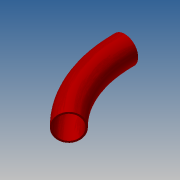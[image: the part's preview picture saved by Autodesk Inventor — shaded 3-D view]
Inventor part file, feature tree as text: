
AUTODESK INVENTOR PART (.ipt)
format: ipt  version: 2017.3 (Build 213257000, 257)  size: 154,112 bytes
history: native  units: in
note: dims shown in document units (in); Inventor stores cm internally (conversion verified against a paired STEP export)
features: other x3, sketch x2, revolve x1, extrude x1
ambient origin geometry x8: Origin, YZ Plane, XZ Plane, XY Plane, X Axis, Y Axis, Z Axis, Center Point
bodies: Solid1 (feature_tree)
feature tree (7):
  other  "A1-19027-100-05 HCWI elbow - female.ipt"
  revolve  "Revolution1"  [1 undecoded]
  extrude  "Extrusion1"  [1 undecoded]
  other  "Solid1::A1-19027-100-05 HCWI elbow - female.ipt"
  other  "TaggingFeature1"
  sketch  "Sketch1"  dims[d0=0.3937in d1=0.3126in]
  sketch  "Sketch2"  dims[d2=0.5in d3=0.5in d4=0.0in d5=0.0in]
note: 2 required parameter values undecoded (feature->parameter linkage not recoverable at this tier; creation-order binding heuristic only, values carry confidence <= 0.55)